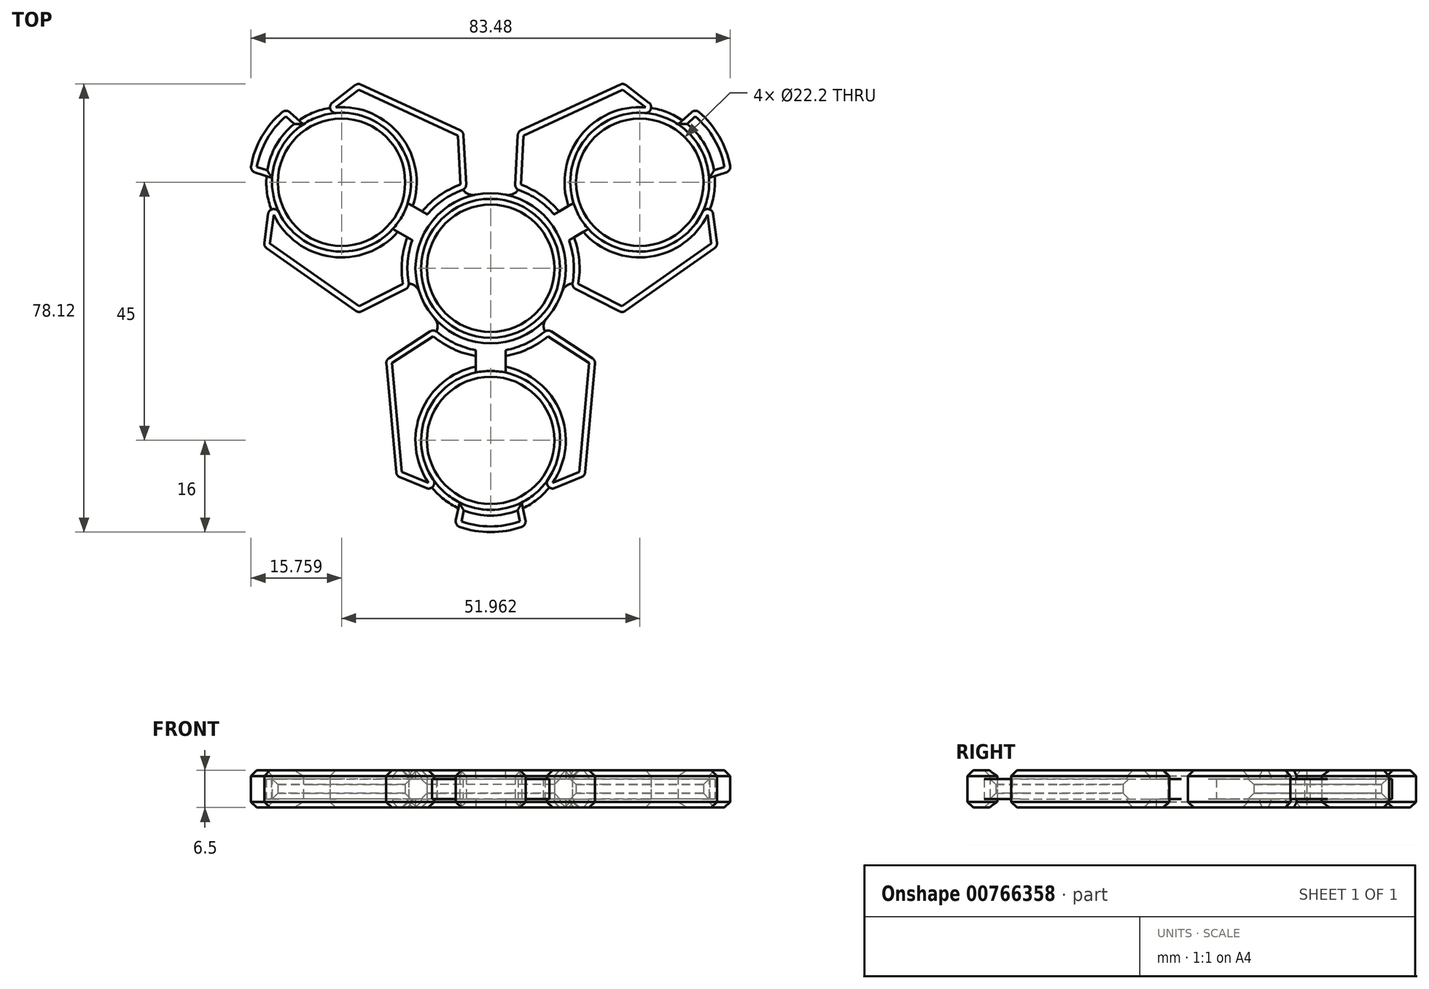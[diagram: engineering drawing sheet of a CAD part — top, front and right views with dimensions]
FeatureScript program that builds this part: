
annotation { "Feature Type Name" : "Feature", "Feature Type Description" : "" }
export const myFeature = defineFeature(function(context is Context, id is Id, definition is map)
    precondition{}
    {
        {
            var Q0;
            Q0=qCreatedBy(makeId("Top.planeOp"),FACE);
            var sketch = newSketch(context, id + "F0", { "sketchPlane" : qUnion([Q0])});
            skCircle(sketch, "E0", {"center": v(0, 0) * mm, "radius": 11.1 * mm});
            skCircle(sketch, "E1.0", {"center": v(0, 0) * mm, "radius": 13.1 * mm});
            skSolve(sketch);
        }
        {
            var Q0;
            Q0=qSketchRegion(id+"F0",true);
            extrude(context, id + "F1", {"entities" : qUnion([Q0]), "depth" : 6.5 * mm, "offsetDistance" : 25 * mm});
        }
        {
            var Q0;
            Q0=qCreatedBy(makeId("Top.planeOp"),FACE);
            var sketch = newSketch(context, id + "F2", { "sketchPlane" : qUnion([Q0])});
            skCircle(sketch, "E2.cCircle", {"center": v(0, 0) * mm, "radius": 30 * mm, "construction": true});
            skLineSegment(sketch, "E2.0", {"start": v(0, -30) * mm, "end": v(-21.21, -21.21) * mm});
            skLineSegment(sketch, "E2.1", {"start": v(-21.21, -21.21) * mm, "end": v(-30, 0) * mm});
            skLineSegment(sketch, "E2.2", {"start": v(-30, 0) * mm, "end": v(-21.21, 21.21) * mm});
            skLineSegment(sketch, "E2.3", {"start": v(-21.21, 21.21) * mm, "end": v(0, 30) * mm});
            skLineSegment(sketch, "E2.4", {"start": v(0, 30) * mm, "end": v(21.21, 21.21) * mm});
            skLineSegment(sketch, "E2.5", {"start": v(21.21, 21.21) * mm, "end": v(30, 0) * mm});
            skLineSegment(sketch, "E2.6", {"start": v(30, 0) * mm, "end": v(21.21, -21.21) * mm});
            skLineSegment(sketch, "E2.7", {"start": v(21.21, -21.21) * mm, "end": v(0, -30) * mm});
            skCircle(sketch, "E3", {"center": v(0, -30) * mm, "radius": 11.1 * mm});
            skCircle(sketch, "E4.0", {"center": v(0, -30) * mm, "radius": 12.1 * mm});
            skLineSegment(sketch, "E5", {"start": v(0, -30) * mm, "end": v(0, -42.1) * mm});
            skLineSegment(sketch, "E6", {"start": v(0, -42.1) * mm, "end": v(18.52, -42.1) * mm});
            skLineSegment(sketch, "E7", {"start": v(25.6, -10.6) * mm, "end": v(30.69, -12.71) * mm});
            skLineSegment(sketch, "E8", {"start": v(30.69, -12.71) * mm, "end": v(18.52, -42.1) * mm});
            skPoint(sketch, "E9.start.orphan", {"position": v(22.4, -42.1) * mm});
            skLineSegment(sketch, "E10.MirrorCS", {"start": v(0, -42.1) * mm, "end": v(-18.52, -42.1) * mm});
            skLineSegment(sketch, "E11.MirrorCS", {"start": v(-30.69, -12.71) * mm, "end": v(-18.52, -42.1) * mm});
            skLineSegment(sketch, "E12.MirrorCS", {"start": v(-25.6, -10.6) * mm, "end": v(-30.69, -12.71) * mm});
            skLineSegment(sketch, "E13", {"start": v(25.6, -10.6) * mm, "end": v(12.1, -5.01) * mm});
            skLineSegment(sketch, "E14", {"start": v(21.21, -8.79) * mm, "end": v(15.36, -42.1) * mm});
            skLineSegment(sketch, "E15.MirrorCS", {"start": v(-21.21, -8.79) * mm, "end": v(-15.36, -42.1) * mm});
            skLineSegment(sketch, "E16.MirrorCS", {"start": v(-25.6, -10.6) * mm, "end": v(-12.1, -5.01) * mm});
            skCircle(sketch, "E17", {"center": v(0, 0) * mm, "radius": 13.1 * mm});
            skLineSegment(sketch, "E18", {"start": v(21.21, -21.21) * mm, "end": v(25.6, -10.6) * mm});
            skLineSegment(sketch, "E19", {"start": v(23.4, -15.9) * mm, "end": v(28.72, -18.1) * mm});
            skLineSegment(sketch, "E20", {"start": v(23.4, -15.9) * mm, "end": v(8.68, -9.8) * mm});
            skLineSegment(sketch, "E21.MirrorCS", {"start": v(-23.4, -15.9) * mm, "end": v(-8.68, -9.8) * mm});
            skLineSegment(sketch, "E22", {"start": v(8.68, -9.8) * mm, "end": v(19.77, -17) * mm});
            skPoint(sketch, "E22.endSnap0", {"position": v(26.07, -17) * mm});
            skLineSegment(sketch, "E23.MirrorCS", {"start": v(-8.68, -9.8) * mm, "end": v(-19.77, -17) * mm});
            skLineSegment(sketch, "E24", {"start": v(18.52, -42.1) * mm, "end": v(13.34, -54.6) * mm});
            skLineSegment(sketch, "E25", {"start": v(6.24, -40.37) * mm, "end": v(17.33, -44.96) * mm});
            skLineSegment(sketch, "E26.MirrorCS", {"start": v(-6.24, -40.37) * mm, "end": v(-17.33, -44.96) * mm});
            skLineSegment(sketch, "E27.MirrorCS", {"start": v(-18.52, -42.1) * mm, "end": v(-13.34, -54.6) * mm});
            skLineSegment(sketch, "E28.MirrorCS", {"start": v(-23.4, -15.9) * mm, "end": v(-28.72, -18.1) * mm});
            skLineSegment(sketch, "E29", {"start": v(15.36, -42.1) * mm, "end": v(13.39, -53.32) * mm});
            skLineSegment(sketch, "E30.MirrorCS", {"start": v(-15.36, -42.1) * mm, "end": v(-13.39, -53.32) * mm});
            skLineSegment(sketch, "E31", {"start": v(6.24, -40.37) * mm, "end": v(16.4, -36.16) * mm});
            skLineSegment(sketch, "E32.MirrorCS", {"start": v(-6.24, -40.37) * mm, "end": v(-16.4, -36.16) * mm});
            skLineSegment(sketch, "E33", {"start": v(0, -17.9) * mm, "end": v(0, -13.1) * mm});
            skLineSegment(sketch, "E34", {"start": v(2.6, -18.18) * mm, "end": v(2.6, -12.84) * mm});
            skLineSegment(sketch, "E35.MirrorCS", {"start": v(-2.6, -18.18) * mm, "end": v(-2.6, -12.84) * mm});
            skCircle(sketch, "E36", {"center": v(0, 0) * mm, "radius": 14.5 * mm});
            skLineSegment(sketch, "E37", {"start": v(8.68, -9.8) * mm, "end": v(8.68, 0) * mm});
            skLineSegment(sketch, "E38", {"start": v(8.68, 0) * mm, "end": v(0, 0) * mm});
            skLineSegment(sketch, "E39", {"start": v(16.4, -36.16) * mm, "end": v(18.23, -16) * mm});
            skPoint(sketch, "E40.orphan", {"position": v(17.02, -15.22) * mm});
            skPoint(sketch, "E41.orphan", {"position": v(-17.02, -15.22) * mm});
            skPoint(sketch, "E42.MirrorCS.start.orphan", {"position": v(-16.4, -36.16) * mm});
            skLineSegment(sketch, "E43.MirrorCS", {"start": v(-16.4, -36.16) * mm, "end": v(-18.23, -16) * mm});
            skCircle(sketch, "E44", {"center": v(0, -30) * mm, "radius": 16 * mm});
            skLineSegment(sketch, "E45", {"start": v(2.73, -41.79) * mm, "end": v(4.06, -45.48) * mm});
            skLineSegment(sketch, "E46.MirrorCS", {"start": v(-2.73, -41.79) * mm, "end": v(-4.06, -45.48) * mm});
            skLineSegment(sketch, "E47", {"start": v(-5.41, -40.82) * mm, "end": v(-6.24, -44.73) * mm});
            skLineSegment(sketch, "E48.MirrorCS", {"start": v(5.41, -40.82) * mm, "end": v(6.24, -44.73) * mm});
            skSolve(sketch);
        }
        {
            var Q0;
            {var subQ0=sQuery(id+"F2.wireOp",EDGE,"E4.0");var subQ1=sQuery(id+"F2.wireOp",EDGE,"E2.0");var subQ2=makeQuery(id+"F2.imprint","INTERSECT",VERTEX,{"derivedFrom":[subQ1,subQ0]});Q0=makeQuery(id+"F2.imprint","IMPRINT",FACE,{"disambiguationData":[TD([[makeQuery(id+"F2.imprint","IMPRINT",EDGE,{"disambiguationData":[TD([[subQ2,-1.0]])],"derivedFrom":subQ1}),-1.0]])]});}
            var Q1;
            {var subQ3=sQuery(id+"F2.wireOp",EDGE,"E2.0");var subQ5=sQuery(id+"F2.wireOp",EDGE,"E4.0");var subQ6=makeQuery(id+"F2.imprint","INTERSECT",VERTEX,{"derivedFrom":[subQ3,subQ5]});Q1=makeQuery(id+"F2.imprint","IMPRINT",FACE,{"disambiguationData":[TD([[makeQuery(id+"F2.imprint","IMPRINT",EDGE,{"disambiguationData":[TD([[subQ6,-1.0]])],"derivedFrom":subQ3}),1.0]])]});}
            var Q2;
            {var subQ5=sQuery(id+"F2.wireOp",EDGE,"E31");Q2=makeQuery(id+"F2.imprint","IMPRINT",FACE,{"disambiguationData":[TD([[makeQuery(id+"F2.imprint","IMPRINT",EDGE,{"derivedFrom":subQ5}),1.0]])]});}
            var Q3;
            {var subQ0=sQuery(id+"F2.wireOp",EDGE,"E39");var subQ8=sQuery(id+"F2.wireOp",EDGE,"E2.7");var subQ11=makeQuery(id+"F2.imprint","INTERSECT",VERTEX,{"derivedFrom":[subQ8,subQ0]});Q3=makeQuery(id+"F2.imprint","IMPRINT",FACE,{"disambiguationData":[TD([[makeQuery(id+"F2.imprint","IMPRINT",EDGE,{"disambiguationData":[TD([[subQ11,-1.0]])],"derivedFrom":subQ8}),-1.0]])]});}
            var Q4;
            {var subQ7=sQuery(id+"F2.wireOp",EDGE,"E44");var subQ9=sQuery(id+"F2.wireOp",EDGE,"E2.0");var subQ10=makeQuery(id+"F2.imprint","INTERSECT",VERTEX,{"derivedFrom":[subQ9,subQ7]});Q4=makeQuery(id+"F2.imprint","IMPRINT",FACE,{"disambiguationData":[TD([[makeQuery(id+"F2.imprint","IMPRINT",EDGE,{"disambiguationData":[TD([[subQ10,-1.0]])],"derivedFrom":subQ9}),-1.0]])]});}
            var Q5;
            {var subQ0=sQuery(id+"F2.wireOp",EDGE,"E44");var subQ1=sQuery(id+"F2.wireOp",EDGE,"E2.0");var subQ2=makeQuery(id+"F2.imprint","INTERSECT",VERTEX,{"derivedFrom":[subQ1,subQ0]});Q5=makeQuery(id+"F2.imprint","IMPRINT",FACE,{"disambiguationData":[TD([[makeQuery(id+"F2.imprint","IMPRINT",EDGE,{"disambiguationData":[TD([[subQ2,-1.0]])],"derivedFrom":subQ1}),1.0]])]});}
            var Q6;
            {var subQ0=sQuery(id+"F2.wireOp",EDGE,"E45");var subQ1=sQuery(id+"F2.wireOp",EDGE,"E44");var subQ2=makeQuery(id+"F2.imprint","INTERSECT",VERTEX,{"derivedFrom":[subQ1,subQ0]});Q6=makeQuery(id+"F2.imprint","IMPRINT",FACE,{"disambiguationData":[TD([[makeQuery(id+"F2.imprint","IMPRINT",EDGE,{"disambiguationData":[TD([[subQ2,1.0]])],"derivedFrom":subQ1}),1.0]])]});}
            var Q7;
            {var subQ1=sQuery(id+"F2.wireOp",EDGE,"E4.0");var subQ3=sQuery(id+"F2.wireOp",EDGE,"E46.MirrorCS");var subQ4=makeQuery(id+"F2.imprint","INTERSECT",VERTEX,{"derivedFrom":[subQ1,subQ3]});Q7=makeQuery(id+"F2.imprint","IMPRINT",FACE,{"disambiguationData":[TD([[makeQuery(id+"F2.imprint","IMPRINT",EDGE,{"disambiguationData":[TD([[subQ4,-1.0]])],"derivedFrom":subQ3}),1.0]])]});}
            var Q8;
            {var subQ1=sQuery(id+"F2.wireOp",EDGE,"E4.0");var subQ3=sQuery(id+"F2.wireOp",EDGE,"E45");var subQ4=makeQuery(id+"F2.imprint","INTERSECT",VERTEX,{"derivedFrom":[subQ1,subQ3]});Q8=makeQuery(id+"F2.imprint","IMPRINT",FACE,{"disambiguationData":[TD([[makeQuery(id+"F2.imprint","IMPRINT",EDGE,{"disambiguationData":[TD([[subQ4,-1.0]])],"derivedFrom":subQ3}),-1.0]])]});}
            var Q9;
            {var subQ0=sQuery(id+"F2.wireOp",EDGE,"E44");var subQ1=sQuery(id+"F2.wireOp",EDGE,"E2.7");var subQ2=makeQuery(id+"F2.imprint","INTERSECT",VERTEX,{"derivedFrom":[subQ1,subQ0]});Q9=makeQuery(id+"F2.imprint","IMPRINT",FACE,{"disambiguationData":[TD([[makeQuery(id+"F2.imprint","IMPRINT",EDGE,{"disambiguationData":[TD([[subQ2,-1.0]])],"derivedFrom":subQ1}),-1.0]])]});}
            var Q10;
            {var subQ0=sQuery(id+"F2.wireOp",EDGE,"E46.MirrorCS");var subQ1=sQuery(id+"F2.wireOp",EDGE,"E10.MirrorCS");var subQ2=makeQuery(id+"F2.imprint","INTERSECT",VERTEX,{"derivedFrom":[subQ1,subQ0]});Q10=makeQuery(id+"F2.imprint","IMPRINT",FACE,{"disambiguationData":[TD([[makeQuery(id+"F2.imprint","IMPRINT",EDGE,{"disambiguationData":[TD([[subQ2,-1.0]])],"derivedFrom":subQ1}),1.0]])]});}
            var Q11;
            {var subQ0=sQuery(id+"F2.wireOp",EDGE,"E45");var subQ1=sQuery(id+"F2.wireOp",EDGE,"E6");var subQ2=makeQuery(id+"F2.imprint","INTERSECT",VERTEX,{"derivedFrom":[subQ1,subQ0]});Q11=makeQuery(id+"F2.imprint","IMPRINT",FACE,{"disambiguationData":[TD([[makeQuery(id+"F2.imprint","IMPRINT",EDGE,{"disambiguationData":[TD([[subQ2,-1.0]])],"derivedFrom":subQ1}),-1.0]])]});}
            var Q12;
            {var subQ0=sQuery(id+"F2.wireOp",EDGE,"E45");var subQ1=sQuery(id+"F2.wireOp",EDGE,"E4.0");var subQ2=makeQuery(id+"F2.imprint","INTERSECT",VERTEX,{"derivedFrom":[subQ1,subQ0]});Q12=makeQuery(id+"F2.imprint","IMPRINT",FACE,{"disambiguationData":[TD([[makeQuery(id+"F2.imprint","IMPRINT",EDGE,{"disambiguationData":[TD([[subQ2,-1.0]])],"derivedFrom":subQ1}),-1.0]])]});}
            var Q13;
            {var subQ0=sQuery(id+"F2.wireOp",EDGE,"E46.MirrorCS");var subQ1=sQuery(id+"F2.wireOp",EDGE,"E4.0");var subQ2=makeQuery(id+"F2.imprint","INTERSECT",VERTEX,{"derivedFrom":[subQ1,subQ0]});Q13=makeQuery(id+"F2.imprint","IMPRINT",FACE,{"disambiguationData":[TD([[makeQuery(id+"F2.imprint","IMPRINT",EDGE,{"disambiguationData":[TD([[subQ2,1.0]])],"derivedFrom":subQ1}),-1.0]])]});}
            extrude(context, id + "F3", {"entities" : qUnion([Q0, Q1, Q2, Q3, Q4, Q5, Q6, Q7, Q8, Q9, Q10, Q11, Q12, Q13]), "depth" : 6.5 * mm, "offsetDistance" : 25 * mm});
        }
        {
            var Q0;
            Q0=makeQuery(id+"F3.opExtrude","SWEPT_EDGE",EDGE,{"disambiguationData":[OSD([sQuery(id+"F2.wireOp",EDGE,"E26.MirrorCS"),sQuery(id+"F2.wireOp",EDGE,"E30.MirrorCS")])]});
            var Q1;
            Q1=makeQuery(id+"F3.opExtrude","SWEPT_EDGE",EDGE,{"disambiguationData":[OSD([sQuery(id+"F2.wireOp",EDGE,"E25"),sQuery(id+"F2.wireOp",EDGE,"E29")])]});
            var Q2;
            Q2=makeQuery(id+"F3.opExtrude","SWEPT_EDGE",EDGE,{"disambiguationData":[OSD([sQuery(id+"F2.wireOp",EDGE,"E44"),sQuery(id+"F2.wireOp",EDGE,"E47")])]});
            var Q3;
            Q3=makeQuery(id+"F3.opExtrude","SWEPT_EDGE",EDGE,{"disambiguationData":[OSD([sQuery(id+"F2.wireOp",EDGE,"E44"),sQuery(id+"F2.wireOp",EDGE,"E48.MirrorCS")])]});
            fillet(context, id + "F4", {"entities" : qUnion([Q0, Q1, Q2, Q3]), "radius" : 1 * mm, "tangentPropagation" : true, "allowEdgeOverflow" : false});
        }
        {
            var Q0;
            Q0=makeQuery(id+"F3.opExtrude","SWEPT_EDGE",EDGE,{"disambiguationData":[OSD([sQuery(id+"F2.wireOp",EDGE,"E15.MirrorCS"),sQuery(id+"F2.wireOp",EDGE,"E23.MirrorCS")])]});
            var Q1;
            Q1=makeQuery(id+"F3.opExtrude","SWEPT_EDGE",EDGE,{"disambiguationData":[OSD([sQuery(id+"F2.wireOp",EDGE,"E14"),sQuery(id+"F2.wireOp",EDGE,"E22")])]});
            var Q2;
            Q2=makeQuery(id+"F3.opExtrude","SWEPT_EDGE",EDGE,{"disambiguationData":[OSD([sQuery(id+"F2.wireOp",EDGE,"E14"),sQuery(id+"F2.wireOp",EDGE,"E31"),sQuery(id+"F2.wireOp",EDGE,"E39")])]});
            var Q3;
            Q3=makeQuery(id+"F3.opExtrude","SWEPT_EDGE",EDGE,{"disambiguationData":[OSD([sQuery(id+"F2.wireOp",EDGE,"E15.MirrorCS"),sQuery(id+"F2.wireOp",EDGE,"E32.MirrorCS"),sQuery(id+"F2.wireOp",EDGE,"E43.MirrorCS")])]});
            fillet(context, id + "F5", {"entities" : qUnion([Q0, Q1, Q2, Q3]), "radius" : 1 * mm, "allowEdgeOverflow" : false});
        }
        {
            var Q0;
            Q0=makeQuery(id+"F1.opExtrude","CAP_EDGE",EDGE,{"disambiguationData":[OSD([sQuery(id+"F0.wireOp",EDGE,"E0")])],"isStart":false});
            var Q1;
            Q1=makeQuery(id+"F1.opExtrude","CAP_EDGE",EDGE,{"disambiguationData":[OSD([sQuery(id+"F0.wireOp",EDGE,"E0")])],"isStart":true});
            var Q2;
            {var subQ0=sQuery(id+"F2.wireOp",EDGE,"E4.0");var subQ1=makeQuery(id+"F2.imprint","INTERSECT",VERTEX,{"derivedFrom":[sQuery(id+"F2.wireOp",EDGE,"E2.7"),subQ0]});Q2=makeQuery(id+"F3.opExtrude","CAP_EDGE",EDGE,{"disambiguationData":[OSD([subQ0]),TDD([makeQuery(id+"F2.imprint","IMPRINT",EDGE,{"disambiguationData":[TD([[makeQuery(id+"F2.imprint","INTERSECT",VERTEX,{"derivedFrom":[subQ0,sQuery(id+"F2.wireOp",EDGE,"E34")]}),1.0]])],"derivedFrom":subQ0}),makeQuery(id+"F2.imprint","IMPRINT",EDGE,{"disambiguationData":[TD([[subQ1,1.0]])],"derivedFrom":subQ0})])],"isStart":false});}
            var Q3;
            {var subQ0=sQuery(id+"F2.wireOp",EDGE,"E4.0");var subQ1=makeQuery(id+"F2.imprint","INTERSECT",VERTEX,{"derivedFrom":[sQuery(id+"F2.wireOp",EDGE,"E2.0"),subQ0]});Q3=makeQuery(id+"F3.opExtrude","CAP_EDGE",EDGE,{"disambiguationData":[OSD([subQ0]),TDD([makeQuery(id+"F2.imprint","IMPRINT",EDGE,{"disambiguationData":[TD([[makeQuery(id+"F2.imprint","INTERSECT",VERTEX,{"derivedFrom":[subQ0,sQuery(id+"F2.wireOp",EDGE,"E35.MirrorCS")]}),-1.0]])],"derivedFrom":subQ0}),makeQuery(id+"F2.imprint","IMPRINT",EDGE,{"disambiguationData":[TD([[subQ1,-1.0]])],"derivedFrom":subQ0})])],"isStart":false});}
            var Q4;
            {var subQ0=sQuery(id+"F2.wireOp",EDGE,"E4.0");var subQ1=makeQuery(id+"F2.imprint","INTERSECT",VERTEX,{"derivedFrom":[sQuery(id+"F2.wireOp",EDGE,"E2.0"),subQ0]});Q4=makeQuery(id+"F3.opExtrude","CAP_EDGE",EDGE,{"disambiguationData":[OSD([subQ0]),TDD([makeQuery(id+"F2.imprint","IMPRINT",EDGE,{"disambiguationData":[TD([[makeQuery(id+"F2.imprint","INTERSECT",VERTEX,{"derivedFrom":[subQ0,sQuery(id+"F2.wireOp",EDGE,"E35.MirrorCS")]}),-1.0]])],"derivedFrom":subQ0}),makeQuery(id+"F2.imprint","IMPRINT",EDGE,{"disambiguationData":[TD([[subQ1,-1.0]])],"derivedFrom":subQ0})])],"isStart":true});}
            var Q5;
            {var subQ0=sQuery(id+"F2.wireOp",EDGE,"E4.0");var subQ1=makeQuery(id+"F2.imprint","INTERSECT",VERTEX,{"derivedFrom":[sQuery(id+"F2.wireOp",EDGE,"E2.7"),subQ0]});Q5=makeQuery(id+"F3.opExtrude","CAP_EDGE",EDGE,{"disambiguationData":[OSD([subQ0]),TDD([makeQuery(id+"F2.imprint","IMPRINT",EDGE,{"disambiguationData":[TD([[makeQuery(id+"F2.imprint","INTERSECT",VERTEX,{"derivedFrom":[subQ0,sQuery(id+"F2.wireOp",EDGE,"E34")]}),1.0]])],"derivedFrom":subQ0}),makeQuery(id+"F2.imprint","IMPRINT",EDGE,{"disambiguationData":[TD([[subQ1,1.0]])],"derivedFrom":subQ0})])],"isStart":true});}
            var Q6;
            Q6=makeQuery(id+"F3.opExtrude","CAP_EDGE",EDGE,{"disambiguationData":[OSD([sQuery(id+"F2.wireOp",EDGE,"E44")])],"isStart":true});
            var Q7;
            Q7=makeQuery(id+"F3.opExtrude","CAP_EDGE",EDGE,{"disambiguationData":[OSD([sQuery(id+"F2.wireOp",EDGE,"E44")])],"isStart":false});
            var Q8;
            {var subQ0=sQuery(id+"F2.wireOp",EDGE,"E4.0");var subQ1=makeQuery(id+"F2.imprint","INTERSECT",VERTEX,{"derivedFrom":[subQ0,sQuery(id+"F2.wireOp",EDGE,"E45")]});var subQ3=makeQuery(id+"F2.imprint","INTERSECT",VERTEX,{"derivedFrom":[subQ0,sQuery(id+"F2.wireOp",EDGE,"E46.MirrorCS")]});Q8=makeQuery(id+"F3.opExtrude","CAP_EDGE",EDGE,{"disambiguationData":[OSD([subQ0]),TDD([makeQuery(id+"F2.imprint","IMPRINT",EDGE,{"disambiguationData":[TD([[subQ3,1.0]])],"derivedFrom":subQ0}),makeQuery(id+"F2.imprint","IMPRINT",EDGE,{"disambiguationData":[TD([[subQ3,-1.0]])],"derivedFrom":subQ0}),makeQuery(id+"F2.imprint","IMPRINT",EDGE,{"disambiguationData":[TD([[subQ1,1.0]])],"derivedFrom":subQ0}),makeQuery(id+"F2.imprint","IMPRINT",EDGE,{"disambiguationData":[TD([[subQ1,-1.0]])],"derivedFrom":subQ0})])],"isStart":false});}
            var Q9;
            {var subQ0=sQuery(id+"F2.wireOp",EDGE,"E4.0");var subQ1=makeQuery(id+"F2.imprint","INTERSECT",VERTEX,{"derivedFrom":[subQ0,sQuery(id+"F2.wireOp",EDGE,"E45")]});var subQ3=makeQuery(id+"F2.imprint","INTERSECT",VERTEX,{"derivedFrom":[subQ0,sQuery(id+"F2.wireOp",EDGE,"E46.MirrorCS")]});Q9=makeQuery(id+"F3.opExtrude","CAP_EDGE",EDGE,{"disambiguationData":[OSD([subQ0]),TDD([makeQuery(id+"F2.imprint","IMPRINT",EDGE,{"disambiguationData":[TD([[subQ3,1.0]])],"derivedFrom":subQ0}),makeQuery(id+"F2.imprint","IMPRINT",EDGE,{"disambiguationData":[TD([[subQ3,-1.0]])],"derivedFrom":subQ0}),makeQuery(id+"F2.imprint","IMPRINT",EDGE,{"disambiguationData":[TD([[subQ1,1.0]])],"derivedFrom":subQ0}),makeQuery(id+"F2.imprint","IMPRINT",EDGE,{"disambiguationData":[TD([[subQ1,-1.0]])],"derivedFrom":subQ0})])],"isStart":true});}
            chamfer(context, id + "F6", {"entities" : qUnion([Q0, Q1, Q2, Q3, Q4, Q5, Q6, Q7, Q8, Q9]), "width" : 1 * mm, "tangentPropagation" : true});
        }
        {
            var Q0;
            Q0=makeQuery(id+"F3.opExtrude","SWEPT_BODY",BODY,{"disambiguationData":[OSD([sQuery(id+"F2.wireOp",EDGE,"E2.0"),sQuery(id+"F2.wireOp",EDGE,"E2.1"),sQuery(id+"F2.wireOp",EDGE,"E2.6"),sQuery(id+"F2.wireOp",EDGE,"E2.7"),sQuery(id+"F2.wireOp",EDGE,"E3"),sQuery(id+"F2.wireOp",EDGE,"E4.0"),sQuery(id+"F2.wireOp",EDGE,"E6"),sQuery(id+"F2.wireOp",EDGE,"E7"),sQuery(id+"F2.wireOp",EDGE,"E8"),sQuery(id+"F2.wireOp",EDGE,"E10.MirrorCS"),sQuery(id+"F2.wireOp",EDGE,"E11.MirrorCS"),sQuery(id+"F2.wireOp",EDGE,"E12.MirrorCS")])]});
            var Q1;
            Q1=makeQuery(id+"F3.opExtrude","SWEPT_BODY",BODY,{"disambiguationData":[OSD([sQuery(id+"F2.wireOp",EDGE,"E4.0"),sQuery(id+"F2.wireOp",EDGE,"E23.MirrorCS"),sQuery(id+"F2.wireOp",EDGE,"E32.MirrorCS"),sQuery(id+"F2.wireOp",EDGE,"E35.MirrorCS"),sQuery(id+"F2.wireOp",EDGE,"E36"),sQuery(id+"F2.wireOp",EDGE,"E43.MirrorCS")])]});
            var Q2;
            Q2=makeQuery(id+"F3.opExtrude","SWEPT_BODY",BODY,{"disambiguationData":[OSD([sQuery(id+"F2.wireOp",EDGE,"E4.0"),sQuery(id+"F2.wireOp",EDGE,"E22"),sQuery(id+"F2.wireOp",EDGE,"E31"),sQuery(id+"F2.wireOp",EDGE,"E34"),sQuery(id+"F2.wireOp",EDGE,"E36"),sQuery(id+"F2.wireOp",EDGE,"E39")])]});
            var Q3;
            {var subQ0=sQuery(id+"F0.wireOp",EDGE,"E0");Q3=makeQuery(id+"F6.opChamfer","BLEND_EDGE",EDGE,{"blendedFrom":[makeQuery(id+"F1.opExtrude","CAP_EDGE",EDGE,{"disambiguationData":[OSD([subQ0])],"isStart":false}),makeQuery(id+"F1.opExtrude","SWEPT_FACE",FACE,{"disambiguationData":[OSD([subQ0])]})],"blendedInto":[makeQuery(id+"F1.opExtrude","SWEPT_FACE",FACE,{"disambiguationData":[OSD([subQ0])]})]});}
            circularPattern(context, id + "F7", {"entities" : qUnion([Q0, Q1, Q2]), "axis" : qUnion([Q3]), "angle" : 360 * degree, "instanceCount" : 3, "equalSpace" : true});
        }
        {
            var Q0;
            Q0=qCreatedBy(makeId("Top.planeOp"),FACE);
            cPlane(context, id + "F8", {"entities" : qUnion([Q0]), "cplaneType" : CPlaneType.OFFSET, "offset" : 1.5 * mm, "width" : 150 * mm, "height" : 150 * mm});
        }
        {
            var Q0;
            Q0=qCreatedBy(id+"F8.planeOp",FACE);
            var sketch = newSketch(context, id + "F9", { "sketchPlane" : qUnion([Q0])});
            skCircle(sketch, "E49", {"center": v(0, 0) * mm, "radius": 30 * mm});
            skCircle(sketch, "E50", {"center": v(0, -30) * mm, "radius": 11.1 * mm});
            skCircle(sketch, "E51.0", {"center": v(0, -30) * mm, "radius": 13.1 * mm});
            skLineSegment(sketch, "E52", {"start": v(0, 0) * mm, "end": v(7.8, 0) * mm});
            skLineSegment(sketch, "E53", {"start": v(7.8, 0) * mm, "end": v(7.8, -9.8) * mm});
            skLineSegment(sketch, "E54", {"start": v(7.8, -9.8) * mm, "end": v(15.37, -15.3) * mm});
            skLineSegment(sketch, "E55", {"start": v(0, 0) * mm, "end": v(0, -7.45) * mm});
            skLineSegment(sketch, "E56.MirrorCS", {"start": v(-7.8, -9.8) * mm, "end": v(-15.37, -15.3) * mm});
            skLineSegment(sketch, "E57", {"start": v(-15.37, -15.3) * mm, "end": v(-8.14, -19.74) * mm});
            skLineSegment(sketch, "E58.MirrorCS", {"start": v(15.37, -15.3) * mm, "end": v(8.14, -19.74) * mm});
            skCircle(sketch, "E59", {"center": v(0, 0) * mm, "radius": 12.53 * mm});
            skSolve(sketch);
        }
        {
            var Q0;
            {var subQ0=sQuery(id+"F9.wireOp",EDGE,"E51.0");var subQ1=sQuery(id+"F9.wireOp",EDGE,"E49");var subQ2=makeQuery(id+"F9.imprint","INTERSECT",VERTEX,{"disambiguationData":[OD(0.0)],"derivedFrom":[subQ1,subQ0]});Q0=makeQuery(id+"F9.imprint","IMPRINT",FACE,{"disambiguationData":[TD([[makeQuery(id+"F9.imprint","IMPRINT",EDGE,{"disambiguationData":[TD([[subQ2,-1.0]])],"derivedFrom":subQ1}),-1.0]])]});}
            var Q1;
            {var subQ0=sQuery(id+"F9.wireOp",EDGE,"E51.0");var subQ1=sQuery(id+"F9.wireOp",EDGE,"E49");var subQ2=makeQuery(id+"F9.imprint","INTERSECT",VERTEX,{"disambiguationData":[OD(0.0)],"derivedFrom":[subQ1,subQ0]});Q1=makeQuery(id+"F9.imprint","IMPRINT",FACE,{"disambiguationData":[TD([[makeQuery(id+"F9.imprint","IMPRINT",EDGE,{"disambiguationData":[TD([[subQ2,-1.0]])],"derivedFrom":subQ1}),1.0]])]});}
            var Q2;
            {var subQ1=sQuery(id+"F9.wireOp",EDGE,"E54");Q2=makeQuery(id+"F9.imprint","IMPRINT",FACE,{"disambiguationData":[TD([[makeQuery(id+"F9.imprint","IMPRINT",EDGE,{"derivedFrom":subQ1}),-1.0]])]});}
            extrude(context, id + "F10", {"entities" : qUnion([Q0, Q1, Q2]), "depth" : 3.5 * mm, "offsetDistance" : 25 * mm});
        }
        {
            var Q0;
            Q0=makeQuery(id+"F10.opExtrude","CAP_EDGE",EDGE,{"disambiguationData":[OSD([sQuery(id+"F9.wireOp",EDGE,"E50")])],"isStart":false});
            var Q1;
            Q1=makeQuery(id+"F10.opExtrude","CAP_EDGE",EDGE,{"disambiguationData":[OSD([sQuery(id+"F9.wireOp",EDGE,"E50")])],"isStart":true});
            chamfer(context, id + "F11", {"entities" : qUnion([Q0, Q1]), "width" : 1 * mm, "tangentPropagation" : true});
        }
        {
            var Q0;
            Q0=makeQuery(id+"F10.opExtrude","SWEPT_BODY",BODY,{"disambiguationData":[OSD([sQuery(id+"F9.wireOp",EDGE,"E50"),sQuery(id+"F9.wireOp",EDGE,"E51.0")])]});
            var Q1;
            Q1=makeQuery(id+"F1.opExtrude","SWEPT_FACE",FACE,{"disambiguationData":[OSD([sQuery(id+"F0.wireOp",EDGE,"E0")])]});
            circularPattern(context, id + "F12", {"entities" : qUnion([Q0]), "axis" : qUnion([Q1]), "angle" : 360 * degree, "instanceCount" : 3, "equalSpace" : true});
        }
        {
            var Q0;
            Q0=makeQuery(id+"F1.opExtrude","SWEPT_BODY",BODY,{"disambiguationData":[OSD([sQuery(id+"F0.wireOp",EDGE,"E0"),sQuery(id+"F0.wireOp",EDGE,"E1.0")])]});
            var Q1;
            Q1=makeQuery(id+"F3.opExtrude","SWEPT_BODY",BODY,{"disambiguationData":[OSD([sQuery(id+"F2.wireOp",EDGE,"E4.0"),sQuery(id+"F2.wireOp",EDGE,"E14"),sQuery(id+"F2.wireOp",EDGE,"E22"),sQuery(id+"F2.wireOp",EDGE,"E31"),sQuery(id+"F2.wireOp",EDGE,"E34"),sQuery(id+"F2.wireOp",EDGE,"E36")])]});
            var Q2;
            Q2=makeQuery(id+"F3.opExtrude","SWEPT_BODY",BODY,{"disambiguationData":[OSD([sQuery(id+"F2.wireOp",EDGE,"E4.0"),sQuery(id+"F2.wireOp",EDGE,"E15.MirrorCS"),sQuery(id+"F2.wireOp",EDGE,"E23.MirrorCS"),sQuery(id+"F2.wireOp",EDGE,"E32.MirrorCS"),sQuery(id+"F2.wireOp",EDGE,"E35.MirrorCS"),sQuery(id+"F2.wireOp",EDGE,"E36")])]});
            var Q3;
            Q3=makeQuery(id+"F10.opExtrude","SWEPT_BODY",BODY,{"disambiguationData":[OSD([sQuery(id+"F9.wireOp",EDGE,"E50"),sQuery(id+"F9.wireOp",EDGE,"E51.0"),sQuery(id+"F9.wireOp",EDGE,"E54"),sQuery(id+"F9.wireOp",EDGE,"E56.MirrorCS"),sQuery(id+"F9.wireOp",EDGE,"E57"),sQuery(id+"F9.wireOp",EDGE,"E58.MirrorCS"),sQuery(id+"F9.wireOp",EDGE,"E59")])]});
            var Q4;
            Q4=makeQuery(id+"F12.opPattern","COPY",BODY,{"derivedFrom":makeQuery(id+"F10.opExtrude","SWEPT_BODY",BODY,{"disambiguationData":[OSD([sQuery(id+"F9.wireOp",EDGE,"E50"),sQuery(id+"F9.wireOp",EDGE,"E51.0"),sQuery(id+"F9.wireOp",EDGE,"E54"),sQuery(id+"F9.wireOp",EDGE,"E56.MirrorCS"),sQuery(id+"F9.wireOp",EDGE,"E57"),sQuery(id+"F9.wireOp",EDGE,"E58.MirrorCS"),sQuery(id+"F9.wireOp",EDGE,"E59")])]}),"instanceName":"1"});
            var Q5;
            Q5=makeQuery(id+"F7.opPattern","COPY",BODY,{"derivedFrom":makeQuery(id+"F3.opExtrude","SWEPT_BODY",BODY,{"disambiguationData":[OSD([sQuery(id+"F2.wireOp",EDGE,"E4.0"),sQuery(id+"F2.wireOp",EDGE,"E14"),sQuery(id+"F2.wireOp",EDGE,"E22"),sQuery(id+"F2.wireOp",EDGE,"E31"),sQuery(id+"F2.wireOp",EDGE,"E34"),sQuery(id+"F2.wireOp",EDGE,"E36")])]}),"instanceName":"1"});
            var Q6;
            Q6=makeQuery(id+"F7.opPattern","COPY",BODY,{"derivedFrom":makeQuery(id+"F3.opExtrude","SWEPT_BODY",BODY,{"disambiguationData":[OSD([sQuery(id+"F2.wireOp",EDGE,"E4.0"),sQuery(id+"F2.wireOp",EDGE,"E15.MirrorCS"),sQuery(id+"F2.wireOp",EDGE,"E23.MirrorCS"),sQuery(id+"F2.wireOp",EDGE,"E32.MirrorCS"),sQuery(id+"F2.wireOp",EDGE,"E35.MirrorCS"),sQuery(id+"F2.wireOp",EDGE,"E36")])]}),"instanceName":"1"});
            var Q7;
            Q7=makeQuery(id+"F7.opPattern","COPY",BODY,{"derivedFrom":makeQuery(id+"F3.opExtrude","SWEPT_BODY",BODY,{"disambiguationData":[OSD([sQuery(id+"F2.wireOp",EDGE,"E4.0"),sQuery(id+"F2.wireOp",EDGE,"E15.MirrorCS"),sQuery(id+"F2.wireOp",EDGE,"E23.MirrorCS"),sQuery(id+"F2.wireOp",EDGE,"E32.MirrorCS"),sQuery(id+"F2.wireOp",EDGE,"E35.MirrorCS"),sQuery(id+"F2.wireOp",EDGE,"E36")])]}),"instanceName":"2"});
            var Q8;
            Q8=makeQuery(id+"F12.opPattern","COPY",BODY,{"derivedFrom":makeQuery(id+"F10.opExtrude","SWEPT_BODY",BODY,{"disambiguationData":[OSD([sQuery(id+"F9.wireOp",EDGE,"E50"),sQuery(id+"F9.wireOp",EDGE,"E51.0"),sQuery(id+"F9.wireOp",EDGE,"E54"),sQuery(id+"F9.wireOp",EDGE,"E56.MirrorCS"),sQuery(id+"F9.wireOp",EDGE,"E57"),sQuery(id+"F9.wireOp",EDGE,"E58.MirrorCS"),sQuery(id+"F9.wireOp",EDGE,"E59")])]}),"instanceName":"2"});
            var Q9;
            Q9=makeQuery(id+"F7.opPattern","COPY",BODY,{"derivedFrom":makeQuery(id+"F3.opExtrude","SWEPT_BODY",BODY,{"disambiguationData":[OSD([sQuery(id+"F2.wireOp",EDGE,"E4.0"),sQuery(id+"F2.wireOp",EDGE,"E14"),sQuery(id+"F2.wireOp",EDGE,"E22"),sQuery(id+"F2.wireOp",EDGE,"E31"),sQuery(id+"F2.wireOp",EDGE,"E34"),sQuery(id+"F2.wireOp",EDGE,"E36")])]}),"instanceName":"2"});
            booleanBodies(context, id + "F13", {"operationType" : BooleanOperationType.UNION, "tools" : qUnion([Q0, Q1, Q2, Q3, Q4, Q5, Q6, Q7, Q8, Q9])});
        }
        {
            var Q0;
            Q0=makeQuery(id+"F13.opBoolean","INTERSECT",EDGE,{"derivedFrom":[makeQuery(id+"F1.opExtrude","SWEPT_FACE",FACE,{"disambiguationData":[OSD([sQuery(id+"F0.wireOp",EDGE,"E1.0")])]}),makeQuery(id+"F10.opExtrude","SWEPT_FACE",FACE,{"disambiguationData":[OSD([sQuery(id+"F9.wireOp",EDGE,"E56.MirrorCS")])]})]});
            var Q1;
            Q1=makeQuery(id+"F13.opBoolean","INTERSECT",EDGE,{"derivedFrom":[makeQuery(id+"F1.opExtrude","SWEPT_FACE",FACE,{"disambiguationData":[OSD([sQuery(id+"F0.wireOp",EDGE,"E1.0")])]}),makeQuery(id+"F10.opExtrude","SWEPT_FACE",FACE,{"disambiguationData":[OSD([sQuery(id+"F9.wireOp",EDGE,"E54")])]})]});
            var Q2;
            Q2=makeQuery(id+"F13.opBoolean","INTERSECT",EDGE,{"derivedFrom":[makeQuery(id+"F1.opExtrude","SWEPT_FACE",FACE,{"disambiguationData":[OSD([sQuery(id+"F0.wireOp",EDGE,"E1.0")])]}),makeQuery(id+"F12.opPattern","COPY",FACE,{"derivedFrom":makeQuery(id+"F10.opExtrude","SWEPT_FACE",FACE,{"disambiguationData":[OSD([sQuery(id+"F9.wireOp",EDGE,"E54")])]}),"instanceName":"2"})]});
            var Q3;
            Q3=makeQuery(id+"F13.opBoolean","INTERSECT",EDGE,{"derivedFrom":[makeQuery(id+"F1.opExtrude","SWEPT_FACE",FACE,{"disambiguationData":[OSD([sQuery(id+"F0.wireOp",EDGE,"E1.0")])]}),makeQuery(id+"F12.opPattern","COPY",FACE,{"derivedFrom":makeQuery(id+"F10.opExtrude","SWEPT_FACE",FACE,{"disambiguationData":[OSD([sQuery(id+"F9.wireOp",EDGE,"E56.MirrorCS")])]}),"instanceName":"1"})]});
            var Q4;
            Q4=makeQuery(id+"F13.opBoolean","INTERSECT",EDGE,{"derivedFrom":[makeQuery(id+"F1.opExtrude","SWEPT_FACE",FACE,{"disambiguationData":[OSD([sQuery(id+"F0.wireOp",EDGE,"E1.0")])]}),makeQuery(id+"F12.opPattern","COPY",FACE,{"derivedFrom":makeQuery(id+"F10.opExtrude","SWEPT_FACE",FACE,{"disambiguationData":[OSD([sQuery(id+"F9.wireOp",EDGE,"E56.MirrorCS")])]}),"instanceName":"2"})]});
            var Q5;
            Q5=makeQuery(id+"F13.opBoolean","INTERSECT",EDGE,{"derivedFrom":[makeQuery(id+"F1.opExtrude","SWEPT_FACE",FACE,{"disambiguationData":[OSD([sQuery(id+"F0.wireOp",EDGE,"E1.0")])]}),makeQuery(id+"F12.opPattern","COPY",FACE,{"derivedFrom":makeQuery(id+"F10.opExtrude","SWEPT_FACE",FACE,{"disambiguationData":[OSD([sQuery(id+"F9.wireOp",EDGE,"E54")])]}),"instanceName":"1"})]});
            fillet(context, id + "F14", {"entities" : qUnion([Q0, Q1, Q2, Q3, Q4, Q5]), "radius" : 2 * mm, "tangentPropagation" : true, "allowEdgeOverflow" : false});
        }
    });
